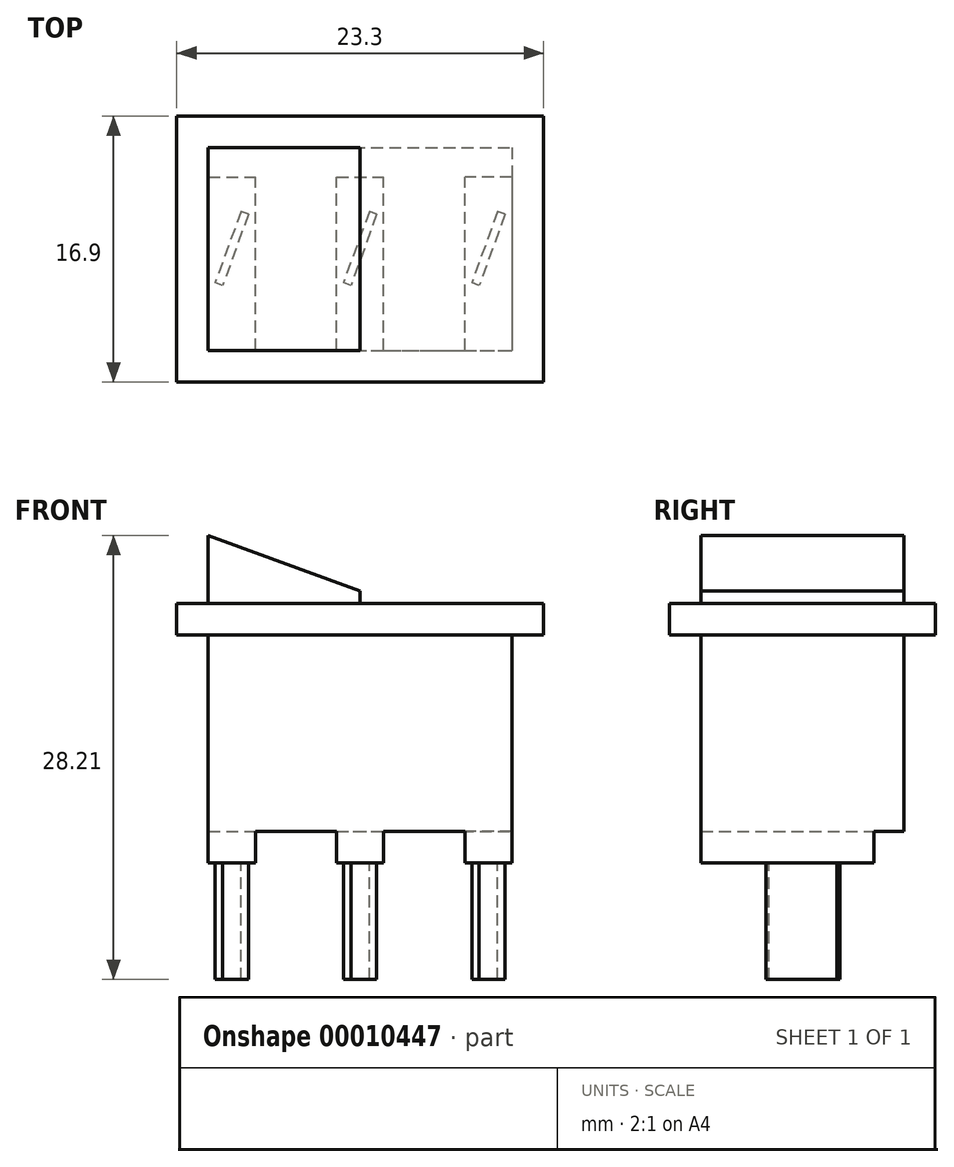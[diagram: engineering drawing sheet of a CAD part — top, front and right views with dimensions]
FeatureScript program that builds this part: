
annotation { "Feature Type Name" : "Feature", "Feature Type Description" : "" }
export const myFeature = defineFeature(function(context is Context, id is Id, definition is map)
    precondition{}
    {
        {
            var Q0;
            Q0=qCreatedBy(makeId("Top.planeOp"),FACE);
            var sketch = newSketch(context, id + "F0", { "sketchPlane" : qUnion([Q0])});
            skLineSegment(sketch, "E0.bottom", {"start": v(-12.09, 6.42) * mm, "end": v(7.21, 6.42) * mm});
            skLineSegment(sketch, "E0.top", {"start": v(-12.09, -6.48) * mm, "end": v(7.21, -6.48) * mm});
            skLineSegment(sketch, "E0.left", {"start": v(-12.09, 6.42) * mm, "end": v(-12.09, -6.48) * mm});
            skLineSegment(sketch, "E0.right", {"start": v(7.21, 6.42) * mm, "end": v(7.21, -6.48) * mm});
            skSolve(sketch);
        }
        {
            var Q0;
            Q0 = qSketchRegion(id + "F0", true);
            extrude(context, id + "F1", {"entities" : qUnion([Q0]), "depth" : 12.5 * mm});
        }
        {
            var Q0;
            Q0=makeQuery(id+"F1.opExtrude","CAP_FACE",FACE,{"disambiguationData":[OSD([sQuery(id+"F0.wireOp",EDGE,"E0.bottom"),sQuery(id+"F0.wireOp",EDGE,"E0.top"),sQuery(id+"F0.wireOp",EDGE,"E0.left"),sQuery(id+"F0.wireOp",EDGE,"E0.right")])],"isStart":false});
            var sketch = newSketch(context, id + "F2", { "sketchPlane" : qUnion([Q0])});
            skLineSegment(sketch, "E1.bottom", {"start": v(-14.09, 8.42) * mm, "end": v(9.21, 8.42) * mm});
            skLineSegment(sketch, "E1.top", {"start": v(-14.09, -8.48) * mm, "end": v(9.21, -8.48) * mm});
            skLineSegment(sketch, "E1.left", {"start": v(-14.09, 8.42) * mm, "end": v(-14.09, -8.48) * mm});
            skLineSegment(sketch, "E1.right", {"start": v(9.21, 8.42) * mm, "end": v(9.21, -8.48) * mm});
            skSolve(sketch);
        }
        {
            var Q0;
            Q0 = qSketchRegion(id + "F2", true);
            extrude(context, id + "F3", {"entities" : qUnion([Q0]), "operationType" : NewBodyOperationType.ADD, "depth" : 2 * mm});
        }
        {
            var Q0;
            Q0=makeQuery(id+"F1.opExtrude","CAP_FACE",FACE,{"disambiguationData":[OSD([sQuery(id+"F0.wireOp",EDGE,"E0.bottom"),sQuery(id+"F0.wireOp",EDGE,"E0.top"),sQuery(id+"F0.wireOp",EDGE,"E0.left"),sQuery(id+"F0.wireOp",EDGE,"E0.right")])],"isStart":true});
            var sketch = newSketch(context, id + "F4", { "sketchPlane" : qUnion([Q0])});
            skLineSegment(sketch, "E2", {"start": v(-12.09, 0.03) * mm, "end": v(7.21, 0.03) * mm, "construction": true});
            skLineSegment(sketch, "E3.bottom", {"start": v(-12.09, 6.48) * mm, "end": v(-9.09, 6.48) * mm});
            skLineSegment(sketch, "E3.top", {"start": v(-12.09, -4.52) * mm, "end": v(-9.09, -4.52) * mm});
            skLineSegment(sketch, "E3.left", {"start": v(-12.09, 6.48) * mm, "end": v(-12.09, -4.52) * mm});
            skLineSegment(sketch, "E3.right", {"start": v(-9.09, 6.48) * mm, "end": v(-9.09, -4.52) * mm});
            skLineSegment(sketch, "E4.bottom", {"start": v(-3.94, 6.48) * mm, "end": v(-0.94, 6.48) * mm});
            skLineSegment(sketch, "E4.top", {"start": v(-3.94, -4.52) * mm, "end": v(-0.94, -4.52) * mm});
            skLineSegment(sketch, "E4.left", {"start": v(-3.94, 6.48) * mm, "end": v(-3.94, -4.52) * mm});
            skLineSegment(sketch, "E4.right", {"start": v(-0.94, 6.48) * mm, "end": v(-0.94, -4.52) * mm});
            skLineSegment(sketch, "E5.bottom", {"start": v(7.21, 6.48) * mm, "end": v(4.21, 6.48) * mm});
            skLineSegment(sketch, "E5.top", {"start": v(7.21, -4.52) * mm, "end": v(4.21, -4.52) * mm});
            skLineSegment(sketch, "E5.left", {"start": v(7.21, 6.48) * mm, "end": v(7.21, -4.52) * mm});
            skLineSegment(sketch, "E5.right", {"start": v(4.21, 6.48) * mm, "end": v(4.21, -4.52) * mm});
            skPoint(sketch, "E6", {"position": v(-2.44, -4.52) * mm});
            skPoint(sketch, "E7", {"position": v(-2.44, 0.03) * mm});
            skSolve(sketch);
        }
        {
            var Q0;
            Q0 = qSketchRegion(id + "F4", true);
            extrude(context, id + "F5", {"entities" : qUnion([Q0]), "operationType" : NewBodyOperationType.ADD, "depth" : 2 * mm});
        }
        {
            var Q0;
            Q0=makeQuery(id+"F5.opExtrude","CAP_FACE",FACE,{"disambiguationData":[OSD([sQuery(id+"F4.wireOp",EDGE,"E3.bottom"),sQuery(id+"F4.wireOp",EDGE,"E3.top"),sQuery(id+"F4.wireOp",EDGE,"E3.left"),sQuery(id+"F4.wireOp",EDGE,"E3.right")])],"isStart":false});
            var sketch = newSketch(context, id + "F6", { "sketchPlane" : qUnion([Q0])});
            skLineSegment(sketch, "E8", {"start": v(-12.09, 0) * mm, "end": v(-9.09, 0) * mm, "construction": true});
            skLineSegment(sketch, "E9.rect.bottom", {"start": v(-9.53, -2.17) * mm, "end": v(-10, -2.34) * mm});
            skLineSegment(sketch, "E9.rect.top", {"start": v(-11.17, 2.34) * mm, "end": v(-11.64, 2.17) * mm});
            skLineSegment(sketch, "E9.rect.left", {"start": v(-9.53, -2.17) * mm, "end": v(-11.17, 2.34) * mm});
            skLineSegment(sketch, "E9.rect.right", {"start": v(-10, -2.34) * mm, "end": v(-11.64, 2.17) * mm});
            skPoint(sketch, "E9.rect.middle", {"position": v(-10.59, 0) * mm});
            skLineSegment(sketch, "E10.1.0.0", {"start": v(-3.02, 2.34) * mm, "end": v(-3.5, 2.17) * mm});
            skLineSegment(sketch, "E10.1.0.1", {"start": v(-1.38, -2.17) * mm, "end": v(-3.02, 2.34) * mm});
            skLineSegment(sketch, "E10.1.0.2", {"start": v(-1.85, -2.34) * mm, "end": v(-3.5, 2.17) * mm});
            skLineSegment(sketch, "E10.1.0.3", {"start": v(-1.38, -2.17) * mm, "end": v(-1.85, -2.34) * mm});
            skLineSegment(sketch, "E10.2.0.0", {"start": v(5.13, 2.34) * mm, "end": v(4.66, 2.17) * mm});
            skLineSegment(sketch, "E10.2.0.1", {"start": v(6.77, -2.17) * mm, "end": v(5.13, 2.34) * mm});
            skLineSegment(sketch, "E10.2.0.2", {"start": v(6.3, -2.34) * mm, "end": v(4.66, 2.17) * mm});
            skLineSegment(sketch, "E10.2.0.3", {"start": v(6.77, -2.17) * mm, "end": v(6.3, -2.34) * mm});
            skLineSegment(sketch, "E10.direction1", {"start": v(-11.64, 2.17) * mm, "end": v(-3.5, 2.17) * mm, "construction": true});
            skSolve(sketch);
        }
        {
            var Q0;
            Q0 = qSketchRegion(id + "F6", true);
            extrude(context, id + "F7", {"entities" : qUnion([Q0]), "operationType" : NewBodyOperationType.ADD, "depth" : 7.4 * mm});
        }
        {
            var Q0;
            Q0=makeQuery(id+"F3.opExtrude","CAP_FACE",FACE,{"disambiguationData":[OSD([sQuery(id+"F2.wireOp",EDGE,"E1.bottom"),sQuery(id+"F2.wireOp",EDGE,"E1.top"),sQuery(id+"F2.wireOp",EDGE,"E1.left"),sQuery(id+"F2.wireOp",EDGE,"E1.right")])],"isStart":false});
            var sketch = newSketch(context, id + "F8", { "sketchPlane" : qUnion([Q0])});
            skLineSegment(sketch, "E11.bottom", {"start": v(-12.09, 6.42) * mm, "end": v(7.21, 6.42) * mm});
            skLineSegment(sketch, "E11.top", {"start": v(-12.09, -6.48) * mm, "end": v(7.21, -6.48) * mm});
            skLineSegment(sketch, "E11.left", {"start": v(-12.09, 6.42) * mm, "end": v(-12.09, -6.48) * mm});
            skLineSegment(sketch, "E11.right", {"start": v(7.21, 6.42) * mm, "end": v(7.21, -6.48) * mm});
            skLineSegment(sketch, "E12", {"start": v(-2.44, 6.42) * mm, "end": v(-2.44, -6.48) * mm});
            skSolve(sketch);
        }
        {
            var Q0;
            {var subQ1=sQuery(id+"F8.wireOp",EDGE,"E11.left");Q0=makeQuery(id+"F8.imprint","IMPRINT",FACE,{"disambiguationData":[TD([[makeQuery(id+"F8.imprint","IMPRINT",EDGE,{"derivedFrom":subQ1}),1.0]])]});}
            extrude(context, id + "F9", {"entities" : qUnion([Q0]), "operationType" : NewBodyOperationType.ADD, "depth" : 5.8 * mm});
        }
        {
            var Q0;
            Q0=makeQuery(id+"F9.opExtrude","CAP_EDGE",EDGE,{"disambiguationData":[OSD([sQuery(id+"F8.wireOp",EDGE,"E12")])],"isStart":false});
            chamfer(context, id + "F10", {"entities" : qUnion([Q0]), "chamferType" : ChamferType.OFFSET_ANGLE, "width" : 5 * mm, "oppositeDirection" : false, "angle" : 70 * degree});
        }
    });
